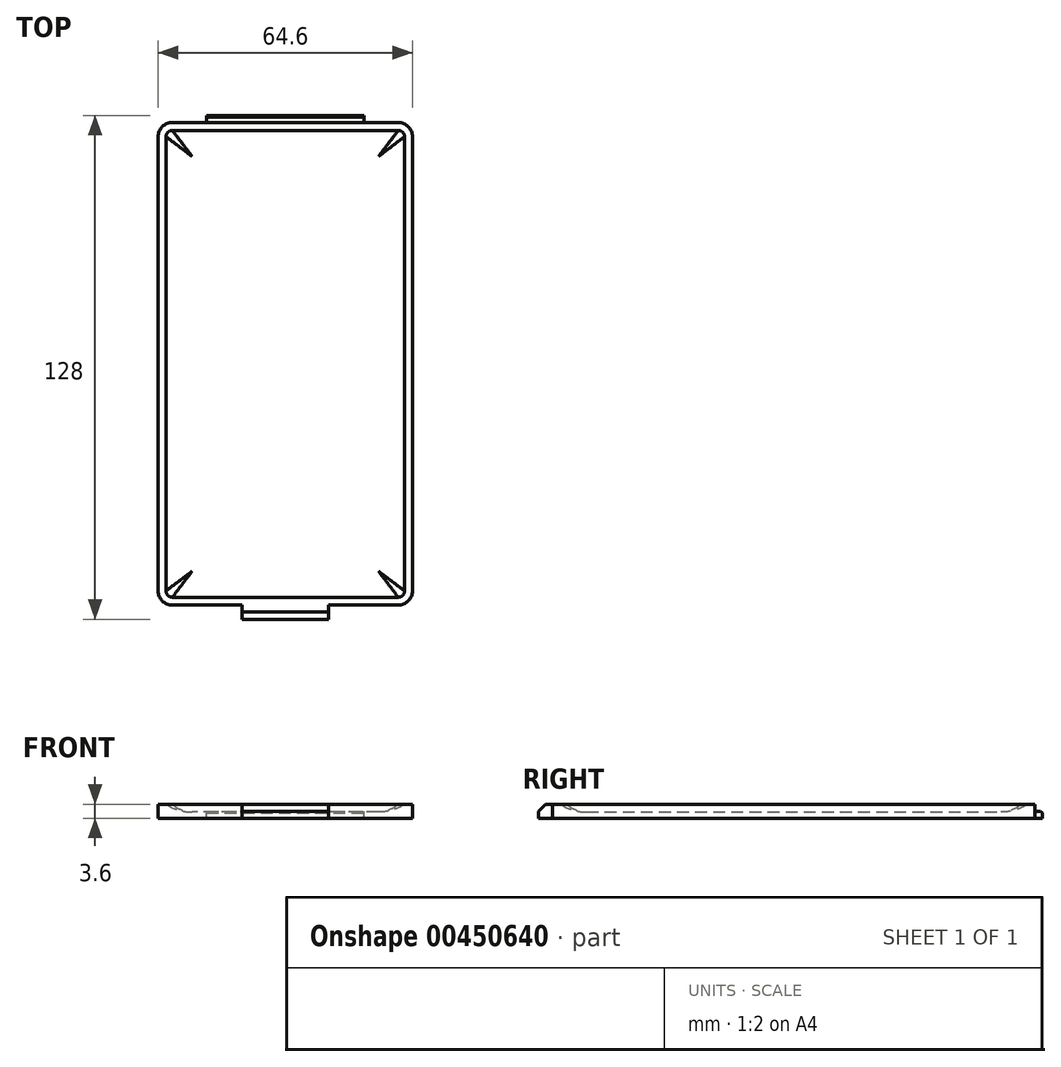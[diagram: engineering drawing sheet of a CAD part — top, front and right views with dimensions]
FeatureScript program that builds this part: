
annotation { "Feature Type Name" : "Feature", "Feature Type Description" : "" }
export const myFeature = defineFeature(function(context is Context, id is Id, definition is map)
    precondition{}
    {
        {
            var Q0;
            Q0=qCreatedBy(makeId("Top.planeOp"),FACE);
            var sketch = newSketch(context, id + "F0", { "sketchPlane" : qUnion([Q0])});
            skLineSegment(sketch, "E0.bottom", {"start": v(32.3, -61.3) * mm, "end": v(-32.3, -61.3) * mm});
            skLineSegment(sketch, "E0.top", {"start": v(32.3, 61.3) * mm, "end": v(-32.3, 61.3) * mm});
            skLineSegment(sketch, "E0.left", {"start": v(32.3, -61.3) * mm, "end": v(32.3, 61.3) * mm});
            skLineSegment(sketch, "E0.right", {"start": v(-32.3, -61.3) * mm, "end": v(-32.3, 61.3) * mm});
            skPoint(sketch, "E0.middle", {"position": v(0, 0) * mm});
            skSolve(sketch);
        }
        {
            var Q0;
            Q0=makeQuery(id+"F0.imprint","IMPRINT",FACE,{"disambiguationData":[TD([[makeQuery(id+"F0.imprint","IMPRINT",EDGE,{"derivedFrom":sQuery(id+"F0.wireOp",EDGE,"E0.bottom")}),-1.0]])]});
            extrude(context, id + "F1", {"entities" : qUnion([Q0]), "depth" : 3.6 * mm});
        }
        {
            var Q0;
            Q0=makeQuery(id+"F1.opExtrude","SWEPT_EDGE",EDGE,{"disambiguationData":[OSD([sQuery(id+"F0.wireOp",EDGE,"E0.bottom"),sQuery(id+"F0.wireOp",EDGE,"E0.left")])]});
            var Q1;
            Q1=makeQuery(id+"F1.opExtrude","SWEPT_EDGE",EDGE,{"disambiguationData":[OSD([sQuery(id+"F0.wireOp",EDGE,"E0.bottom"),sQuery(id+"F0.wireOp",EDGE,"E0.right")])]});
            var Q2;
            Q2=makeQuery(id+"F1.opExtrude","SWEPT_EDGE",EDGE,{"disambiguationData":[OSD([sQuery(id+"F0.wireOp",EDGE,"E0.top"),sQuery(id+"F0.wireOp",EDGE,"E0.left")])]});
            var Q3;
            Q3=makeQuery(id+"F1.opExtrude","SWEPT_EDGE",EDGE,{"disambiguationData":[OSD([sQuery(id+"F0.wireOp",EDGE,"E0.top"),sQuery(id+"F0.wireOp",EDGE,"E0.right")])]});
            fillet(context, id + "F2", {"entities" : qUnion([Q0, Q1, Q2, Q3]), "radius" : 3.6 * mm, "tangentPropagation" : true, "allowEdgeOverflow" : false});
        }
        {
            var Q0;
            Q0=makeQuery(id+"F1.opExtrude","SWEPT_FACE",FACE,{"disambiguationData":[OSD([sQuery(id+"F0.wireOp",EDGE,"E0.bottom")])]});
            var sketch = newSketch(context, id + "F3", { "sketchPlane" : qUnion([Q0])});
            skLineSegment(sketch, "E1.bottom", {"start": v(11, 0) * mm, "end": v(-11, 0) * mm});
            skLineSegment(sketch, "E1.top", {"start": v(11, 3.6) * mm, "end": v(-11, 3.6) * mm});
            skLineSegment(sketch, "E1.left", {"start": v(11, 0) * mm, "end": v(11, 3.6) * mm});
            skLineSegment(sketch, "E1.right", {"start": v(-11, 0) * mm, "end": v(-11, 3.6) * mm});
            skPoint(sketch, "E1.middle", {"position": v(0, 1.8) * mm});
            skPoint(sketch, "E1.middle.positionSnap0", {"position": v(28.7, 1.8) * mm});
            skPoint(sketch, "E1.centerSnap0", {"position": v(28.7, 1.8) * mm});
            skSolve(sketch);
        }
        {
            var Q0;
            Q0=makeQuery(id+"F3.imprint","IMPRINT",FACE,{"disambiguationData":[TD([[makeQuery(id+"F3.imprint","IMPRINT",EDGE,{"derivedFrom":sQuery(id+"F3.wireOp",EDGE,"E1.bottom")}),-1.0]])]});
            extrude(context, id + "F4", {"entities" : qUnion([Q0]), "operationType" : NewBodyOperationType.ADD, "depth" : 3.6 * mm});
        }
        {
            var Q0;
            Q0=makeQuery(id+"F4.opExtrude","CAP_EDGE",EDGE,{"disambiguationData":[OSD([sQuery(id+"F3.wireOp",EDGE,"E1.top")])],"isStart":false});
            chamfer(context, id + "F5", {"entities" : qUnion([Q0]), "width" : 1.8 * mm, "tangentPropagation" : true});
        }
        {
            var Q0;
            Q0=makeQuery(id+"F1.opExtrude","SWEPT_FACE",FACE,{"disambiguationData":[OSD([sQuery(id+"F0.wireOp",EDGE,"E0.top")])]});
            var sketch = newSketch(context, id + "F6", { "sketchPlane" : qUnion([Q0])});
            skLineSegment(sketch, "E2.bottom", {"start": v(20, 0) * mm, "end": v(-20, 0) * mm});
            skLineSegment(sketch, "E2.top", {"start": v(20, 1.8) * mm, "end": v(-20, 1.8) * mm});
            skLineSegment(sketch, "E2.left", {"start": v(20, 0) * mm, "end": v(20, 1.8) * mm});
            skLineSegment(sketch, "E2.right", {"start": v(-20, 0) * mm, "end": v(-20, 1.8) * mm});
            skPoint(sketch, "E2.middle", {"position": v(0, 0.9) * mm});
            skSolve(sketch);
        }
        {
            var Q0;
            Q0=makeQuery(id+"F6.imprint","IMPRINT",FACE,{"disambiguationData":[TD([[makeQuery(id+"F6.imprint","IMPRINT",EDGE,{"derivedFrom":sQuery(id+"F6.wireOp",EDGE,"E2.bottom")}),1.0]])]});
            extrude(context, id + "F7", {"entities" : qUnion([Q0]), "operationType" : NewBodyOperationType.ADD, "depth" : 1.8 * mm});
        }
        {
            var Q0;
            Q0=makeQuery(id+"F7.opExtrude","CAP_EDGE",EDGE,{"disambiguationData":[OSD([sQuery(id+"F6.wireOp",EDGE,"E2.top")])],"isStart":false});
            chamfer(context, id + "F8", {"entities" : qUnion([Q0]), "width" : .4 * mm, "tangentPropagation" : true});
        }
        {
            var Q0;
            Q0=makeQuery(id+"F4.boolean.opBoolean","MERGE",FACE,{"derivedFrom":[makeQuery(id+"F1.opExtrude","CAP_FACE",FACE,{"disambiguationData":[OSD([sQuery(id+"F0.wireOp",EDGE,"E0.bottom"),sQuery(id+"F0.wireOp",EDGE,"E0.top"),sQuery(id+"F0.wireOp",EDGE,"E0.left"),sQuery(id+"F0.wireOp",EDGE,"E0.right")])],"isStart":false}),makeQuery(id+"F4.opExtrude","SWEPT_FACE",FACE,{"disambiguationData":[OSD([sQuery(id+"F3.wireOp",EDGE,"E1.top")])]})]});
            var sketch = newSketch(context, id + "F9", { "sketchPlane" : qUnion([Q0])});
            skArc(sketch, "E3.1", {"start": v(-30.3, -57.7) * mm, "mid": v(-29.83, -58.83) * mm, "end": v(-28.7, -59.3) * mm});
            skLineSegment(sketch, "E3.2", {"start": v(-30.3, -57.7) * mm, "end": v(-30.3, 57.7) * mm});
            skArc(sketch, "E3.3", {"start": v(-28.7, 59.3) * mm, "mid": v(-29.83, 58.83) * mm, "end": v(-30.3, 57.7) * mm});
            skLineSegment(sketch, "E3.4", {"start": v(28.7, 59.3) * mm, "end": v(-28.7, 59.3) * mm});
            skArc(sketch, "E3.6", {"start": v(28.7, -59.3) * mm, "mid": v(29.83, -58.83) * mm, "end": v(30.3, -57.7) * mm});
            skLineSegment(sketch, "E3.7", {"start": v(30.3, -57.7) * mm, "end": v(30.3, 57.7) * mm});
            skArc(sketch, "E3.8", {"start": v(30.3, 57.7) * mm, "mid": v(29.83, 58.83) * mm, "end": v(28.7, 59.3) * mm});
            skLineSegment(sketch, "E4", {"start": v(-28.7, -59.3) * mm, "end": v(28.7, -59.3) * mm});
            skSolve(sketch);
        }
        {
            var Q0;
            Q0=makeQuery(id+"F9.imprint","IMPRINT",FACE,{"disambiguationData":[TD([[makeQuery(id+"F9.imprint","IMPRINT",EDGE,{"derivedFrom":sQuery(id+"F9.wireOp",EDGE,"E3.1")}),1.0]])]});
            extrude(context, id + "F10", {"entities" : qUnion([Q0]), "operationType" : NewBodyOperationType.REMOVE, "oppositeDirection" : true, "depth" : 2 * mm});
        }
        {
            var Q0;
            Q0=makeQuery(id+"F10.boolean.opBoolean","COPY",FACE,{"derivedFrom":makeQuery(id+"F10.opExtrude","CAP_FACE",FACE,{"disambiguationData":[OSD([sQuery(id+"F9.wireOp",EDGE,"E3.1"),sQuery(id+"F9.wireOp",EDGE,"E3.2"),sQuery(id+"F9.wireOp",EDGE,"E3.3"),sQuery(id+"F9.wireOp",EDGE,"E3.4"),sQuery(id+"F9.wireOp",EDGE,"E3.6"),sQuery(id+"F9.wireOp",EDGE,"E3.7"),sQuery(id+"F9.wireOp",EDGE,"E3.8"),sQuery(id+"F9.wireOp",EDGE,"E4")])],"isStart":false})});
            fillet(context, id + "F11", {"entities" : qUnion([Q0]), "radius" : 12 * mm, "tangentPropagation" : true, "allowEdgeOverflow" : false});
        }
    });
